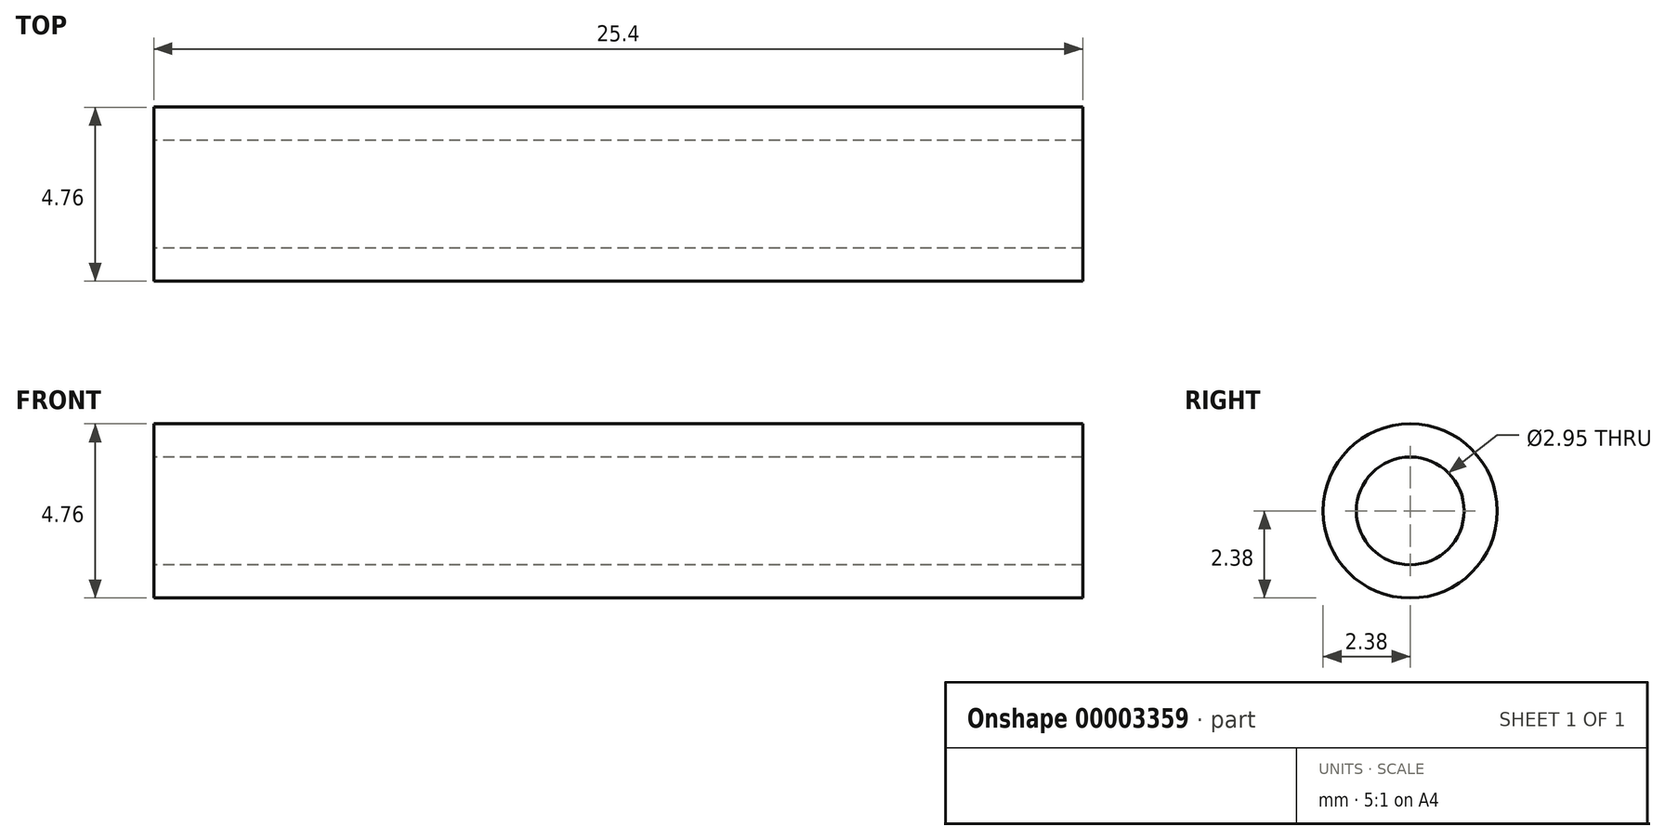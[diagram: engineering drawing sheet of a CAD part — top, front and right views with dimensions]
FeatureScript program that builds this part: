
annotation { "Feature Type Name" : "Feature", "Feature Type Description" : "" }
export const myFeature = defineFeature(function(context is Context, id is Id, definition is map)
    precondition{}
    {
        {
            var Q0;
            Q0=qCreatedBy(makeId("Right.planeOp"),FACE);
            var sketch = newSketch(context, id + "F0", { "sketchPlane" : qUnion([Q0])});
            skCircle(sketch, "E0", {"center": v(0, 0) * mm, "radius": 2.38 * mm});
            skCircle(sketch, "E1", {"center": v(0, 0) * mm, "radius": 1.47 * mm});
            skSolve(sketch);
        }
        {
            var Q0;
            Q0 = qSketchRegion(id + "F0", true);
            extrude(context, id + "F1", {"entities" : qUnion([Q0]), "endBound" : BoundingType.SYMMETRIC, "depth" : 25.4 * mm});
        }
    });
